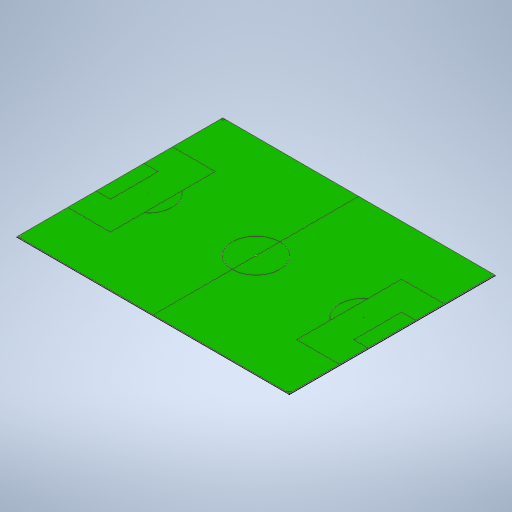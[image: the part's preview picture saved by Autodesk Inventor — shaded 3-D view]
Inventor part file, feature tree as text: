
AUTODESK INVENTOR PART (.ipt)
format: ipt  version: 2024.1 (Build 281209000, 209)  size: 449,024 bytes
history: native  units: in
note: dims shown in document units (in); Inventor stores cm internally (conversion verified against a paired STEP export)
features: sketch x2, extrude x2
ambient origin geometry x8: Origin, YZ Plane, XZ Plane, XY Plane, X Axis, Y Axis, Z Axis, Center Point
bodies: Solid13 (feature_tree)
feature tree (4):
  sketch  "Sketch2"  dims[d210=10.0in d211=0.0in d212=10.0in d213=0.0in]
  sketch  "3D Sketch1"
  extrude  "Extrusion68"  Depth=10.0in TaperAngle=0.0deg
  extrude  "Extrusion69"  [1 undecoded]
note: 1 required parameter value undecoded (feature->parameter linkage not recoverable at this tier; creation-order binding heuristic only, values carry confidence <= 0.55)
